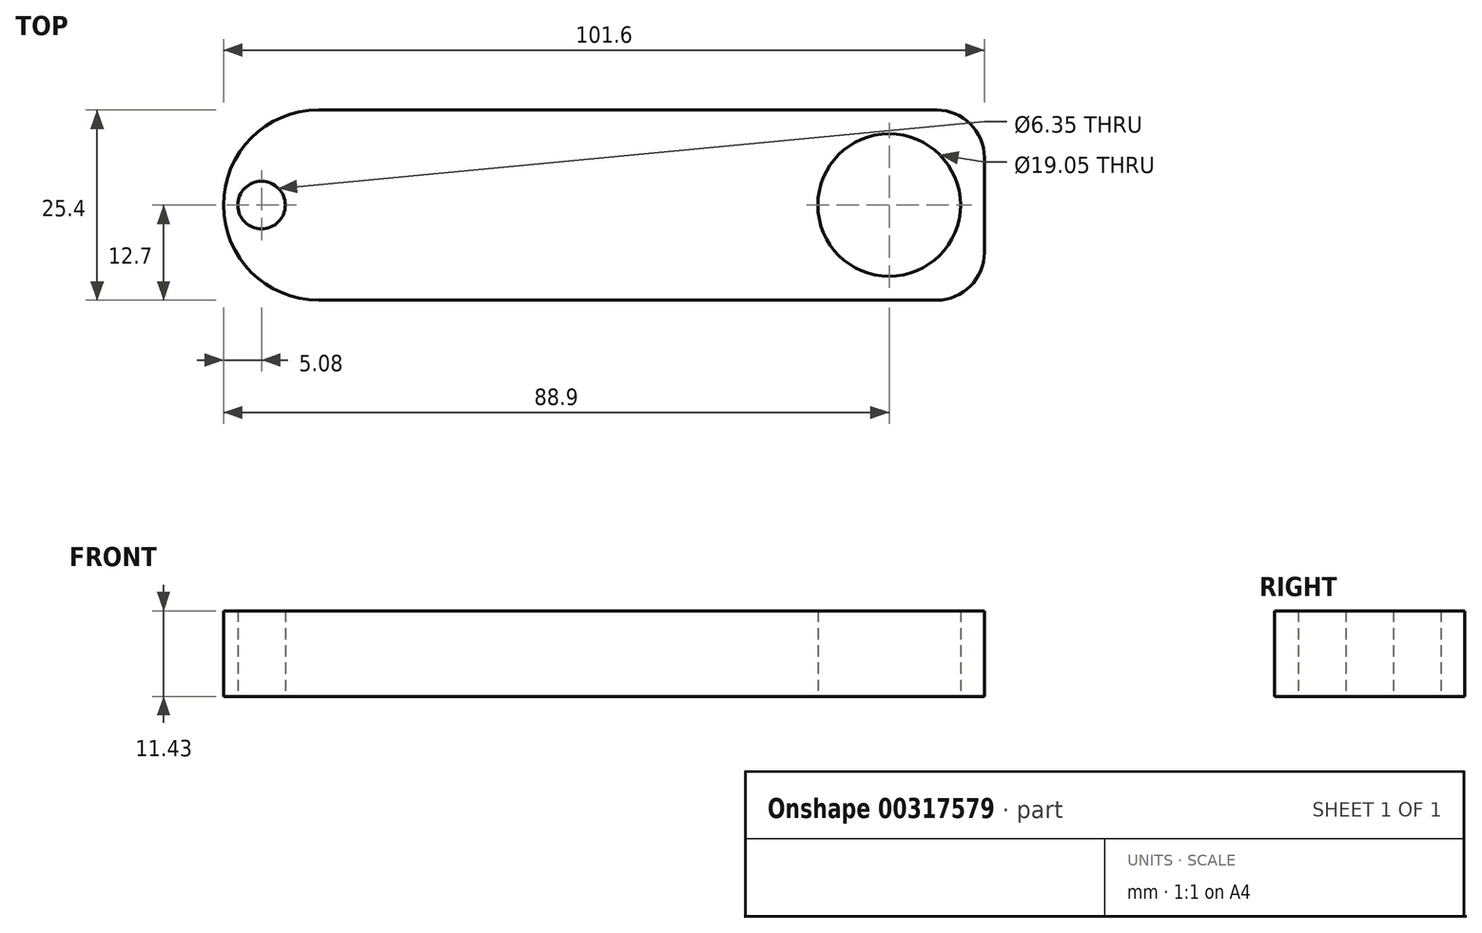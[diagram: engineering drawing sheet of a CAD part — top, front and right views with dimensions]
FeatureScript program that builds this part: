
annotation { "Feature Type Name" : "Feature", "Feature Type Description" : "" }
export const myFeature = defineFeature(function(context is Context, id is Id, definition is map)
    precondition{}
    {
        {
            var Q0;
            Q0=qCreatedBy(makeId("Top.planeOp"),FACE);
            var sketch = newSketch(context, id + "F0", { "sketchPlane" : qUnion([Q0])});
            skLineSegment(sketch, "E0.bottom", {"start": v(-38.1, 12.7) * mm, "end": v(44.45, 12.7) * mm});
            skLineSegment(sketch, "E0.top", {"start": v(-38.1, -12.7) * mm, "end": v(44.45, -12.7) * mm});
            skLineSegment(sketch, "E0.left", {"start": v(-50.8, 0) * mm, "end": v(-50.8, 0) * mm});
            skLineSegment(sketch, "E0.right", {"start": v(50.8, 6.35) * mm, "end": v(50.8, -6.35) * mm});
            skCircle(sketch, "E1", {"center": v(-45.72, 0) * mm, "radius": 3.18 * mm});
            skCircle(sketch, "E2", {"center": v(38.1, 0) * mm, "radius": 9.53 * mm});
            skPoint(sketch, "E3.visualSharp", {"position": v(-50.8, 12.7) * mm});
            skArc(sketch, "E3.filletArc", {"start": v(-38.1, 12.7) * mm, "mid": v(-47.08, 8.98) * mm, "end": v(-50.8, 0) * mm});
            skPoint(sketch, "E4.visualSharp", {"position": v(-50.8, -12.7) * mm});
            skArc(sketch, "E4.filletArc", {"start": v(-50.8, 0) * mm, "mid": v(-47.08, -8.98) * mm, "end": v(-38.1, -12.7) * mm});
            skPoint(sketch, "E5.visualSharp", {"position": v(50.8, -12.7) * mm});
            skArc(sketch, "E5.filletArc", {"start": v(44.45, -12.7) * mm, "mid": v(48.94, -10.84) * mm, "end": v(50.8, -6.35) * mm});
            skPoint(sketch, "E6.visualSharp", {"position": v(50.8, 12.7) * mm});
            skArc(sketch, "E6.filletArc", {"start": v(50.8, 6.35) * mm, "mid": v(48.94, 10.84) * mm, "end": v(44.45, 12.7) * mm});
            skSolve(sketch);
        }
        {
            var Q0;
            Q0=makeQuery(id+"F0.imprint","IMPRINT",FACE,{"disambiguationData":[TD([[makeQuery(id+"F0.imprint","IMPRINT",EDGE,{"derivedFrom":sQuery(id+"F0.wireOp",EDGE,"E0.bottom")}),-1.0]])]});
            extrude(context, id + "F1", {"entities" : qUnion([Q0]), "depth" : 11.43 * mm, "offsetDistance" : 25.4 * mm});
        }
    });
